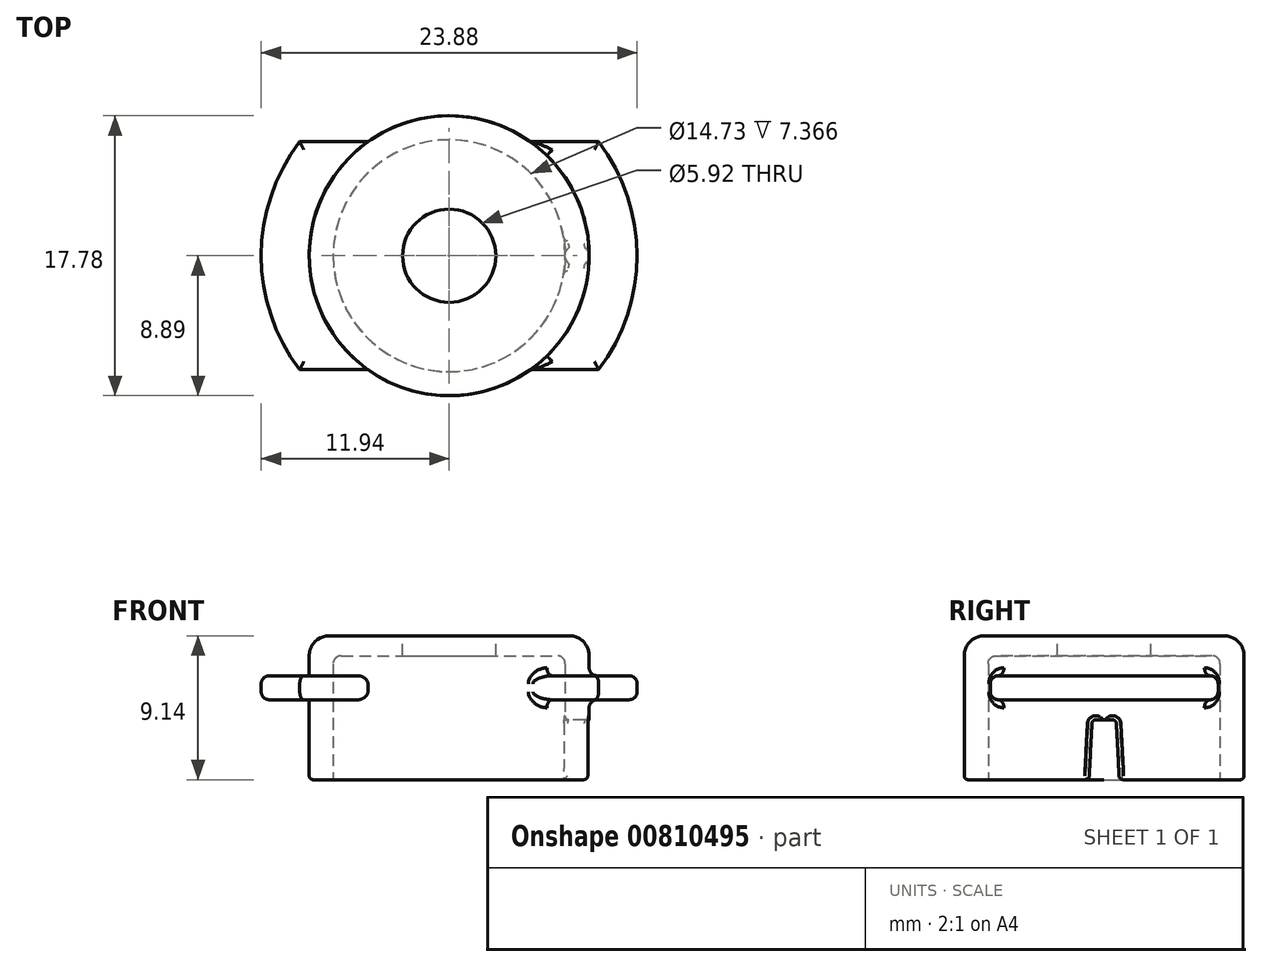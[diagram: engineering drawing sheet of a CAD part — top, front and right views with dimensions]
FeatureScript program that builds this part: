
annotation { "Feature Type Name" : "Feature", "Feature Type Description" : "" }
export const myFeature = defineFeature(function(context is Context, id is Id, definition is map)
    precondition{}
    {
        {
            var Q0;
            Q0=qCreatedBy(makeId("Top.planeOp"),FACE);
            var sketch = newSketch(context, id + "F0", { "sketchPlane" : qUnion([Q0])});
            skCircle(sketch, "E0", {"center": v(0, 0) * mm, "radius": 11.94 * mm});
            skSolve(sketch);
        }
        {
            var Q0;
            Q0=makeQuery(id+"F0.imprint","IMPRINT",FACE,{"disambiguationData":[TD([[makeQuery(id+"F0.imprint","IMPRINT",EDGE,{"derivedFrom":sQuery(id+"F0.wireOp",EDGE,"E0")}),1.0]])]});
            var sketch = newSketch(context, id + "F1", { "sketchPlane" : qUnion([Q0])});
            skLineSegment(sketch, "E1", {"start": v(9.5, 7.24) * mm, "end": v(-9.5, 7.24) * mm});
            skLineSegment(sketch, "E2", {"start": v(9.5, -7.24) * mm, "end": v(-9.5, -7.24) * mm});
            skLineSegment(sketch, "E3", {"start": v(-9.5, 7.24) * mm, "end": v(-9.5, -7.24) * mm, "construction": true});
            skLineSegment(sketch, "E4", {"start": v(9.5, 7.24) * mm, "end": v(9.5, -7.24) * mm, "construction": true});
            skSolve(sketch);
        }
        {
            var Q0;
            Q0=qSketchRegion(id+"F0",true);
            extrude(context, id + "F2", {"entities" : qUnion([Q0]), "depth" : 1.52 * mm, "offsetDistance" : 25.4 * mm});
        }
        {
            var Q0;
            {var subQ0=sQuery(id+"F1.wireOp",EDGE,"E1");Q0=makeQuery(id+"F1.imprint","IMPRINT",FACE,{"disambiguationData":[TD([[makeQuery(id+"F1.imprint","IMPRINT",EDGE,{"derivedFrom":subQ0}),-1.0]])]});}
            var Q1;
            {var subQ0=sQuery(id+"F1.wireOp",EDGE,"E2");Q1=makeQuery(id+"F1.imprint","IMPRINT",FACE,{"disambiguationData":[TD([[makeQuery(id+"F1.imprint","IMPRINT",EDGE,{"derivedFrom":subQ0}),1.0]])]});}
            extrude(context, id + "F3", {"entities" : qUnion([Q0, Q1]), "operationType" : NewBodyOperationType.REMOVE, "depth" : 2.54 * mm, "offsetDistance" : 25.4 * mm, "hasSecondDirection" : true, "secondDirectionOppositeDirection" : true, "secondDirectionDepth" : 25.4 * mm});
        }
        {
            var Q0;
            Q0=makeQuery(id+"F2.opExtrude","CAP_FACE",FACE,{"disambiguationData":[OSD([sQuery(id+"F0.wireOp",EDGE,"E0")])],"isStart":true});
            var sketch = newSketch(context, id + "F4", { "sketchPlane" : qUnion([Q0])});
            skCircle(sketch, "E5", {"center": v(0, 0) * mm, "radius": 8.9 * mm});
            skSolve(sketch);
        }
        {
            var Q0;
            Q0=qSketchRegion(id+"F4",true);
            extrude(context, id + "F5", {"entities" : qUnion([Q0]), "operationType" : NewBodyOperationType.ADD, "oppositeDirection" : true, "depth" : 1.52 * mm, "offsetDistance" : 25.4 * mm});
        }
        {
            var Q0;
            Q0=makeQuery(id+"F5.boolean.opBoolean","MERGE",FACE,{"derivedFrom":[makeQuery(id+"F2.opExtrude","CAP_FACE",FACE,{"disambiguationData":[OSD([sQuery(id+"F0.wireOp",EDGE,"E0")])],"isStart":true}),makeQuery(id+"F5.opExtrude","CAP_FACE",FACE,{"disambiguationData":[OSD([sQuery(id+"F4.wireOp",EDGE,"E5")])],"isStart":true})]});
            var sketch = newSketch(context, id + "F6", { "sketchPlane" : qUnion([Q0])});
            skCircle(sketch, "E6", {"center": v(0, 0) * mm, "radius": 8.9 * mm});
            skSolve(sketch);
        }
        {
            var Q0;
            Q0=qSketchRegion(id+"F6",true);
            extrude(context, id + "F7", {"entities" : qUnion([Q0]), "operationType" : NewBodyOperationType.ADD, "depth" : 5.08 * mm, "offsetDistance" : 25.4 * mm});
        }
        {
            var Q0;
            Q0=makeQuery(id+"F7.opExtrude","CAP_FACE",FACE,{"disambiguationData":[OSD([sQuery(id+"F6.wireOp",EDGE,"E6")])],"isStart":false});
            var sketch = newSketch(context, id + "F8", { "sketchPlane" : qUnion([Q0])});
            skCircle(sketch, "E7", {"center": v(0, 0) * mm, "radius": 7.37 * mm});
            skSolve(sketch);
        }
        {
            var Q0;
            Q0=qSketchRegion(id+"F8",true);
            extrude(context, id + "F9", {"entities" : qUnion([Q0]), "operationType" : NewBodyOperationType.REMOVE, "oppositeDirection" : true, "depth" : 5.08 * mm, "offsetDistance" : 25.4 * mm});
        }
        {
            var Q0;
            Q0=qCreatedBy(makeId("Front.planeOp"),FACE);
            var sketch = newSketch(context, id + "F10", { "sketchPlane" : qUnion([Q0])});
            skLineSegment(sketch, "E8", {"start": v(0, 0) * mm, "end": v(0, -7.62) * mm, "construction": true});
            skSolve(sketch);
        }
        {
            var Q0;
            Q0=makeQuery(id+"F9.boolean.opBoolean","COPY",FACE,{"derivedFrom":makeQuery(id+"F9.opExtrude","CAP_FACE",FACE,{"disambiguationData":[OSD([sQuery(id+"F8.wireOp",EDGE,"E7")])],"isStart":false})});
            var sketch = newSketch(context, id + "F11", { "sketchPlane" : qUnion([Q0])});
            skCircle(sketch, "E9", {"center": v(0, 0) * mm, "radius": 7.37 * mm});
            skSolve(sketch);
        }
        {
            var Q0;
            Q0=makeQuery(id+"F5.boolean.opBoolean","MERGE",FACE,{"derivedFrom":[makeQuery(id+"F2.opExtrude","CAP_FACE",FACE,{"disambiguationData":[OSD([sQuery(id+"F0.wireOp",EDGE,"E0")])],"isStart":false}),makeQuery(id+"F5.opExtrude","CAP_FACE",FACE,{"disambiguationData":[OSD([sQuery(id+"F4.wireOp",EDGE,"E5")])],"isStart":false})]});
            var sketch = newSketch(context, id + "F12", { "sketchPlane" : qUnion([Q0])});
            skCircle(sketch, "E10", {"center": v(0, 0) * mm, "radius": 8.9 * mm});
            skSolve(sketch);
        }
        {
            var Q0;
            Q0 = qSketchRegion(id + "F12", true);
            extrude(context, id + "F13", {"entities" : qUnion([Q0]), "operationType" : NewBodyOperationType.ADD, "depth" : 2.54 * mm, "offsetDistance" : 25.4 * mm});
        }
        {
            var Q0;
            Q0=makeQuery(id+"F13.opExtrude","CAP_FACE",FACE,{"disambiguationData":[OSD([sQuery(id+"F12.wireOp",EDGE,"E10")])],"isStart":false});
            var sketch = newSketch(context, id + "F14", { "sketchPlane" : qUnion([Q0])});
            skCircle(sketch, "E11", {"center": v(0, 0) * mm, "radius": 2.96 * mm});
            skSolve(sketch);
        }
        {
            var Q0;
            Q0 = qSketchRegion(id + "F14", true);
            extrude(context, id + "F15", {"entities" : qUnion([Q0]), "operationType" : NewBodyOperationType.REMOVE, "oppositeDirection" : true, "depth" : 25.4 * mm, "offsetDistance" : 25.4 * mm, "hasSecondDirection" : true, "secondDirectionOppositeDirection" : false, "secondDirectionDepth" : 25.4 * mm});
        }
        {
            var Q0;
            Q0=makeQuery(id+"F5.boolean.opBoolean","SPLIT",EDGE,{"disambiguationData":[OD(1.0)],"derivedFrom":makeQuery(id+"F3.boolean.opBoolean","INTERSECT",EDGE,{"derivedFrom":[makeQuery(id+"F2.opExtrude","CAP_FACE",FACE,{"disambiguationData":[OSD([sQuery(id+"F0.wireOp",EDGE,"E0")])],"isStart":false}),makeQuery(id+"F3.opExtrude","SWEPT_FACE",FACE,{"disambiguationData":[OSD([sQuery(id+"F1.wireOp",EDGE,"E2")])]})]})});
            var Q1;
            Q1=makeQuery(id+"F5.boolean.opBoolean","SPLIT",EDGE,{"disambiguationData":[OD(1.0)],"derivedFrom":makeQuery(id+"F3.boolean.opBoolean","INTERSECT",EDGE,{"derivedFrom":[makeQuery(id+"F2.opExtrude","CAP_FACE",FACE,{"disambiguationData":[OSD([sQuery(id+"F0.wireOp",EDGE,"E0")])],"isStart":true}),makeQuery(id+"F3.opExtrude","SWEPT_FACE",FACE,{"disambiguationData":[OSD([sQuery(id+"F1.wireOp",EDGE,"E2")])]})]})});
            var Q2;
            Q2=makeQuery(id+"F3.boolean.opBoolean","SPLIT",EDGE,{"disambiguationData":[OD(1.0)],"derivedFrom":makeQuery(id+"F2.opExtrude","CAP_EDGE",EDGE,{"disambiguationData":[OSD([sQuery(id+"F0.wireOp",EDGE,"E0")])],"isStart":true})});
            var Q3;
            Q3=makeQuery(id+"F3.boolean.opBoolean","SPLIT",EDGE,{"disambiguationData":[OD(1.0)],"derivedFrom":makeQuery(id+"F2.opExtrude","CAP_EDGE",EDGE,{"disambiguationData":[OSD([sQuery(id+"F0.wireOp",EDGE,"E0")])],"isStart":false})});
            var Q4;
            Q4=makeQuery(id+"F5.boolean.opBoolean","SPLIT",EDGE,{"disambiguationData":[OD(1.0)],"derivedFrom":makeQuery(id+"F3.boolean.opBoolean","INTERSECT",EDGE,{"derivedFrom":[makeQuery(id+"F2.opExtrude","CAP_FACE",FACE,{"disambiguationData":[OSD([sQuery(id+"F0.wireOp",EDGE,"E0")])],"isStart":true}),makeQuery(id+"F3.opExtrude","SWEPT_FACE",FACE,{"disambiguationData":[OSD([sQuery(id+"F1.wireOp",EDGE,"E1")])]})]})});
            var Q5;
            Q5=makeQuery(id+"F5.boolean.opBoolean","SPLIT",EDGE,{"disambiguationData":[OD(1.0)],"derivedFrom":makeQuery(id+"F3.boolean.opBoolean","INTERSECT",EDGE,{"derivedFrom":[makeQuery(id+"F2.opExtrude","CAP_FACE",FACE,{"disambiguationData":[OSD([sQuery(id+"F0.wireOp",EDGE,"E0")])],"isStart":false}),makeQuery(id+"F3.opExtrude","SWEPT_FACE",FACE,{"disambiguationData":[OSD([sQuery(id+"F1.wireOp",EDGE,"E1")])]})]})});
            var Q6;
            Q6=makeQuery(id+"F5.boolean.opBoolean","SPLIT",EDGE,{"disambiguationData":[OD(0.0)],"derivedFrom":makeQuery(id+"F3.boolean.opBoolean","INTERSECT",EDGE,{"derivedFrom":[makeQuery(id+"F2.opExtrude","CAP_FACE",FACE,{"disambiguationData":[OSD([sQuery(id+"F0.wireOp",EDGE,"E0")])],"isStart":true}),makeQuery(id+"F3.opExtrude","SWEPT_FACE",FACE,{"disambiguationData":[OSD([sQuery(id+"F1.wireOp",EDGE,"E2")])]})]})});
            var Q7;
            Q7=makeQuery(id+"F5.boolean.opBoolean","SPLIT",EDGE,{"disambiguationData":[OD(0.0)],"derivedFrom":makeQuery(id+"F3.boolean.opBoolean","INTERSECT",EDGE,{"derivedFrom":[makeQuery(id+"F2.opExtrude","CAP_FACE",FACE,{"disambiguationData":[OSD([sQuery(id+"F0.wireOp",EDGE,"E0")])],"isStart":false}),makeQuery(id+"F3.opExtrude","SWEPT_FACE",FACE,{"disambiguationData":[OSD([sQuery(id+"F1.wireOp",EDGE,"E2")])]})]})});
            var Q8;
            Q8=makeQuery(id+"F3.boolean.opBoolean","SPLIT",EDGE,{"disambiguationData":[OD(0.0)],"derivedFrom":makeQuery(id+"F2.opExtrude","CAP_EDGE",EDGE,{"disambiguationData":[OSD([sQuery(id+"F0.wireOp",EDGE,"E0")])],"isStart":true})});
            var Q9;
            Q9=makeQuery(id+"F3.boolean.opBoolean","SPLIT",EDGE,{"disambiguationData":[OD(0.0)],"derivedFrom":makeQuery(id+"F2.opExtrude","CAP_EDGE",EDGE,{"disambiguationData":[OSD([sQuery(id+"F0.wireOp",EDGE,"E0")])],"isStart":false})});
            var Q10;
            Q10=makeQuery(id+"F5.boolean.opBoolean","SPLIT",EDGE,{"disambiguationData":[OD(0.0)],"derivedFrom":makeQuery(id+"F3.boolean.opBoolean","INTERSECT",EDGE,{"derivedFrom":[makeQuery(id+"F2.opExtrude","CAP_FACE",FACE,{"disambiguationData":[OSD([sQuery(id+"F0.wireOp",EDGE,"E0")])],"isStart":false}),makeQuery(id+"F3.opExtrude","SWEPT_FACE",FACE,{"disambiguationData":[OSD([sQuery(id+"F1.wireOp",EDGE,"E1")])]})]})});
            var Q11;
            Q11=makeQuery(id+"F5.boolean.opBoolean","SPLIT",EDGE,{"disambiguationData":[OD(0.0)],"derivedFrom":makeQuery(id+"F3.boolean.opBoolean","INTERSECT",EDGE,{"derivedFrom":[makeQuery(id+"F2.opExtrude","CAP_FACE",FACE,{"disambiguationData":[OSD([sQuery(id+"F0.wireOp",EDGE,"E0")])],"isStart":true}),makeQuery(id+"F3.opExtrude","SWEPT_FACE",FACE,{"disambiguationData":[OSD([sQuery(id+"F1.wireOp",EDGE,"E1")])]})]})});
            fillet(context, id + "F16", {"entities" : qUnion([Q0, Q1, Q2, Q3, Q4, Q5, Q6, Q7, Q8, Q9, Q10, Q11]), "radius" : 0.5 * mm, "tangentPropagation" : true, "allowEdgeOverflow" : false});
        }
        {
            var Q0;
            Q0=makeQuery(id+"F13.opExtrude","CAP_EDGE",EDGE,{"disambiguationData":[OSD([sQuery(id+"F12.wireOp",EDGE,"E10")])],"isStart":false});
            fillet(context, id + "F17", {"entities" : qUnion([Q0]), "radius" : 1.27 * mm, "tangentPropagation" : true, "allowEdgeOverflow" : false});
        }
        {
            var Q0;
            Q0=makeQuery(id+"F11.imprint","IMPRINT",FACE,{"disambiguationData":[TD([[makeQuery(id+"F11.imprint","IMPRINT",EDGE,{"derivedFrom":sQuery(id+"F11.wireOp",EDGE,"E9")}),1.0]])]});
            var sketch = newSketch(context, id + "F18", { "sketchPlane" : qUnion([Q0])});
            skCircle(sketch, "E12", {"center": v(0, 0) * mm, "radius": 7.37 * mm});
            skSolve(sketch);
        }
        {
            var Q0;
            Q0 = qSketchRegion(id + "F18", true);
            extrude(context, id + "F19", {"entities" : qUnion([Q0]), "operationType" : NewBodyOperationType.REMOVE, "oppositeDirection" : true, "depth" : 2.8 * mm, "offsetDistance" : 25.4 * mm});
        }
        {
            var Q0;
            Q0=makeQuery(id+"F13.opExtrude","CAP_FACE",FACE,{"disambiguationData":[OSD([sQuery(id+"F12.wireOp",EDGE,"E10")])],"isStart":false});
            cPlane(context, id + "F20", {"entities" : qUnion([Q0]), "cplaneType" : CPlaneType.OFFSET, "offset" : 5.33 * mm, "oppositeDirection" : true, "width" : 152.4 * mm, "height" : 152.4 * mm});
        }
        {
            var Q0;
            Q0=qCreatedBy(id+"F20.planeOp",FACE);
            var sketch = newSketch(context, id + "F21", { "sketchPlane" : qUnion([Q0])});
            skLineSegment(sketch, "E13", {"start": v(8.86, 0.76) * mm, "end": v(7.33, 0.76) * mm});
            skLineSegment(sketch, "E14", {"start": v(8.86, -0.76) * mm, "end": v(7.33, -0.76) * mm});
            skLineSegment(sketch, "E15", {"start": v(0, 0) * mm, "end": v(8.9, 0) * mm, "construction": true});
            skArc(sketch, "E16", {"start": v(7.33, 0.76) * mm, "mid": v(7.37, 0) * mm, "end": v(7.33, -0.76) * mm});
            skArc(sketch, "E17", {"start": v(8.86, 0.76) * mm, "mid": v(8.9, 0) * mm, "end": v(8.86, -0.76) * mm});
            skSolve(sketch);
        }
        {
            var Q0;
            Q0 = qSketchRegion(id + "F21", true);
            extrude(context, id + "F22", {"entities" : qUnion([Q0]), "operationType" : NewBodyOperationType.REMOVE, "oppositeDirection" : true, "depth" : 25.4 * mm, "offsetDistance" : 25.4 * mm, "hasDraft" : true, "draftAngle" : 3 * degree});
        }
        {
            var Q0;
            Q0=makeQuery(id+"F22.boolean.opBoolean","COPY",EDGE,{"derivedFrom":makeQuery(id+"F22.opExtrude","CAP_EDGE",EDGE,{"disambiguationData":[OSD([sQuery(id+"F21.wireOp",EDGE,"E17")])],"isStart":true})});
            var Q1;
            {var subQ2=sQuery(id+"F4.wireOp",EDGE,"E5");var subQ6=makeQuery(id+"F5.opExtrude","SWEPT_FACE",FACE,{"disambiguationData":[OSD([subQ2])]});Q1=makeQuery(id+"F22.boolean.opBoolean","INTERSECT",EDGE,{"derivedFrom":[makeQuery(id+"F13.boolean.opBoolean","MERGE",FACE,{"derivedFrom":[makeQuery(id+"F7.boolean.opBoolean","MERGE",FACE,{"derivedFrom":[makeQuery(id+"F5.boolean.opBoolean","SPLIT",FACE,{"disambiguationData":[TD([makeQuery(id+"F3.boolean.opBoolean","COPY",FACE,{"derivedFrom":makeQuery(id+"F3.opExtrude","SWEPT_FACE",FACE,{"disambiguationData":[OSD([sQuery(id+"F1.wireOp",EDGE,"E1")])]})})])],"derivedFrom":subQ6}),makeQuery(id+"F5.boolean.opBoolean","SPLIT",FACE,{"disambiguationData":[TD([makeQuery(id+"F3.boolean.opBoolean","COPY",FACE,{"derivedFrom":makeQuery(id+"F3.opExtrude","SWEPT_FACE",FACE,{"disambiguationData":[OSD([sQuery(id+"F1.wireOp",EDGE,"E2")])]})})])],"derivedFrom":subQ6}),makeQuery(id+"F7.opExtrude","SWEPT_FACE",FACE,{"disambiguationData":[OSD([sQuery(id+"F6.wireOp",EDGE,"E6")])]})]}),makeQuery(id+"F13.opExtrude","SWEPT_FACE",FACE,{"disambiguationData":[OSD([sQuery(id+"F12.wireOp",EDGE,"E10")])]})]}),makeQuery(id+"F22.opExtrude","SWEPT_FACE",FACE,{"disambiguationData":[OSD([sQuery(id+"F21.wireOp",EDGE,"E14")])]})]});}
            var Q2;
            {var subQ2=sQuery(id+"F4.wireOp",EDGE,"E5");var subQ6=makeQuery(id+"F5.opExtrude","SWEPT_FACE",FACE,{"disambiguationData":[OSD([subQ2])]});Q2=makeQuery(id+"F22.boolean.opBoolean","INTERSECT",EDGE,{"derivedFrom":[makeQuery(id+"F13.boolean.opBoolean","MERGE",FACE,{"derivedFrom":[makeQuery(id+"F7.boolean.opBoolean","MERGE",FACE,{"derivedFrom":[makeQuery(id+"F5.boolean.opBoolean","SPLIT",FACE,{"disambiguationData":[TD([makeQuery(id+"F3.boolean.opBoolean","COPY",FACE,{"derivedFrom":makeQuery(id+"F3.opExtrude","SWEPT_FACE",FACE,{"disambiguationData":[OSD([sQuery(id+"F1.wireOp",EDGE,"E1")])]})})])],"derivedFrom":subQ6}),makeQuery(id+"F5.boolean.opBoolean","SPLIT",FACE,{"disambiguationData":[TD([makeQuery(id+"F3.boolean.opBoolean","COPY",FACE,{"derivedFrom":makeQuery(id+"F3.opExtrude","SWEPT_FACE",FACE,{"disambiguationData":[OSD([sQuery(id+"F1.wireOp",EDGE,"E2")])]})})])],"derivedFrom":subQ6}),makeQuery(id+"F7.opExtrude","SWEPT_FACE",FACE,{"disambiguationData":[OSD([sQuery(id+"F6.wireOp",EDGE,"E6")])]})]}),makeQuery(id+"F13.opExtrude","SWEPT_FACE",FACE,{"disambiguationData":[OSD([sQuery(id+"F12.wireOp",EDGE,"E10")])]})]}),makeQuery(id+"F22.opExtrude","SWEPT_FACE",FACE,{"disambiguationData":[OSD([sQuery(id+"F21.wireOp",EDGE,"E13")])]})]});}
            var Q3;
            Q3=makeQuery(id+"F22.boolean.opBoolean","INTERSECT",EDGE,{"derivedFrom":[makeQuery(id+"F19.boolean.opBoolean","MERGE",FACE,{"derivedFrom":[makeQuery(id+"F9.boolean.opBoolean","COPY",FACE,{"derivedFrom":makeQuery(id+"F9.opExtrude","SWEPT_FACE",FACE,{"disambiguationData":[OSD([sQuery(id+"F8.wireOp",EDGE,"E7")])]})}),makeQuery(id+"F19.opExtrude","SWEPT_FACE",FACE,{"disambiguationData":[OSD([sQuery(id+"F18.wireOp",EDGE,"E12")])]})]}),makeQuery(id+"F22.opExtrude","SWEPT_FACE",FACE,{"disambiguationData":[OSD([sQuery(id+"F21.wireOp",EDGE,"E14")])]})]});
            var Q4;
            Q4=makeQuery(id+"F22.boolean.opBoolean","INTERSECT",EDGE,{"derivedFrom":[makeQuery(id+"F19.boolean.opBoolean","MERGE",FACE,{"derivedFrom":[makeQuery(id+"F9.boolean.opBoolean","COPY",FACE,{"derivedFrom":makeQuery(id+"F9.opExtrude","SWEPT_FACE",FACE,{"disambiguationData":[OSD([sQuery(id+"F8.wireOp",EDGE,"E7")])]})}),makeQuery(id+"F19.opExtrude","SWEPT_FACE",FACE,{"disambiguationData":[OSD([sQuery(id+"F18.wireOp",EDGE,"E12")])]})]}),makeQuery(id+"F22.opExtrude","SWEPT_FACE",FACE,{"disambiguationData":[OSD([sQuery(id+"F21.wireOp",EDGE,"E13")])]})]});
            var Q5;
            Q5=makeQuery(id+"F22.boolean.opBoolean","COPY",EDGE,{"derivedFrom":makeQuery(id+"F22.opExtrude","CAP_EDGE",EDGE,{"disambiguationData":[OSD([sQuery(id+"F21.wireOp",EDGE,"E16")])],"isStart":true})});
            var Q6;
            Q6=makeQuery(id+"F22.boolean.opBoolean","COPY",EDGE,{"derivedFrom":makeQuery(id+"F22.opExtrude","CAP_EDGE",EDGE,{"disambiguationData":[OSD([sQuery(id+"F21.wireOp",EDGE,"E14")])],"isStart":true})});
            var Q7;
            Q7=makeQuery(id+"F22.boolean.opBoolean","COPY",EDGE,{"derivedFrom":makeQuery(id+"F22.opExtrude","CAP_EDGE",EDGE,{"disambiguationData":[OSD([sQuery(id+"F21.wireOp",EDGE,"E13")])],"isStart":true})});
            var Q8;
            Q8=makeQuery(id+"F22.boolean.opBoolean","INTERSECT",EDGE,{"derivedFrom":[makeQuery(id+"F7.opExtrude","CAP_FACE",FACE,{"disambiguationData":[OSD([sQuery(id+"F6.wireOp",EDGE,"E6")])],"isStart":false}),makeQuery(id+"F22.opExtrude","SWEPT_FACE",FACE,{"disambiguationData":[OSD([sQuery(id+"F21.wireOp",EDGE,"E14")])]})]});
            var Q9;
            Q9=makeQuery(id+"F22.boolean.opBoolean","INTERSECT",EDGE,{"derivedFrom":[makeQuery(id+"F7.opExtrude","CAP_FACE",FACE,{"disambiguationData":[OSD([sQuery(id+"F6.wireOp",EDGE,"E6")])],"isStart":false}),makeQuery(id+"F22.opExtrude","SWEPT_FACE",FACE,{"disambiguationData":[OSD([sQuery(id+"F21.wireOp",EDGE,"E13")])]})]});
            fillet(context, id + "F23", {"entities" : qUnion([Q0, Q1, Q2, Q3, Q4, Q5, Q6, Q7, Q8, Q9]), "radius" : 0.25 * mm, "tangentPropagation" : true, "allowEdgeOverflow" : false});
        }
        {
            var Q0;
            {var subQ1=sQuery(id+"F8.wireOp",EDGE,"E7");Q0=makeQuery(id+"FQYb2V3vegdUbzZ_1.1.F22.boolean.opBoolean","SPLIT",EDGE,{"disambiguationData":[TD([makeQuery(id+"FQYb2V3vegdUbzZ_1.1.F22.opExtrude","SWEPT_FACE",FACE,{"disambiguationData":[OSD([sQuery(id+"F21.wireOp",EDGE,"E13")])]})])],"derivedFrom":makeQuery(id+"F9.boolean.opBoolean","COPY",EDGE,{"derivedFrom":makeQuery(id+"F9.opExtrude","CAP_EDGE",EDGE,{"disambiguationData":[OSD([subQ1])],"isStart":true})})});}
            var Q1;
            {var subQ1=sQuery(id+"F6.wireOp",EDGE,"E6");Q1=makeQuery(id+"FQYb2V3vegdUbzZ_1.1.F22.boolean.opBoolean","SPLIT",EDGE,{"disambiguationData":[TD([makeQuery(id+"FQYb2V3vegdUbzZ_1.1.F22.opExtrude","SWEPT_FACE",FACE,{"disambiguationData":[OSD([sQuery(id+"F21.wireOp",EDGE,"E13")])]})])],"derivedFrom":makeQuery(id+"F7.opExtrude","CAP_EDGE",EDGE,{"disambiguationData":[OSD([subQ1])],"isStart":false})});}
            var Q2;
            {var subQ1=sQuery(id+"F21.wireOp",EDGE,"E14");var subQ3=sQuery(id+"F8.wireOp",EDGE,"E7");var subQ5=sQuery(id+"F21.wireOp",EDGE,"E13");Q2=makeQuery(id+"FQYb2V3vegdUbzZ_1.2.F22.boolean.opBoolean","SPLIT",EDGE,{"disambiguationData":[TD([makeQuery(id+"FQYb2V3vegdUbzZ_1.2.F22.opExtrude","SWEPT_FACE",FACE,{"disambiguationData":[OSD([subQ5])]})])],"derivedFrom":makeQuery(id+"FQYb2V3vegdUbzZ_1.1.F22.boolean.opBoolean","SPLIT",EDGE,{"disambiguationData":[TD([makeQuery(id+"FQYb2V3vegdUbzZ_1.1.F22.opExtrude","SWEPT_FACE",FACE,{"disambiguationData":[OSD([subQ1])]})])],"derivedFrom":makeQuery(id+"F9.boolean.opBoolean","COPY",EDGE,{"derivedFrom":makeQuery(id+"F9.opExtrude","CAP_EDGE",EDGE,{"disambiguationData":[OSD([subQ3])],"isStart":true})})})});}
            var Q3;
            {var subQ2=sQuery(id+"F6.wireOp",EDGE,"E6");var subQ7=sQuery(id+"F21.wireOp",EDGE,"E13");var subQ8=sQuery(id+"F21.wireOp",EDGE,"E14");Q3=makeQuery(id+"FQYb2V3vegdUbzZ_1.2.F22.boolean.opBoolean","SPLIT",EDGE,{"disambiguationData":[TD([makeQuery(id+"FQYb2V3vegdUbzZ_1.2.F22.opExtrude","SWEPT_FACE",FACE,{"disambiguationData":[OSD([subQ7])]})])],"derivedFrom":makeQuery(id+"FQYb2V3vegdUbzZ_1.1.F22.boolean.opBoolean","SPLIT",EDGE,{"disambiguationData":[TD([makeQuery(id+"FQYb2V3vegdUbzZ_1.1.F22.opExtrude","SWEPT_FACE",FACE,{"disambiguationData":[OSD([subQ8])]})])],"derivedFrom":makeQuery(id+"F7.opExtrude","CAP_EDGE",EDGE,{"disambiguationData":[OSD([subQ2])],"isStart":false})})});}
            var Q4;
            {var subQ2=sQuery(id+"F6.wireOp",EDGE,"E6");var subQ4=sQuery(id+"F21.wireOp",EDGE,"E13");var subQ8=sQuery(id+"F21.wireOp",EDGE,"E14");Q4=makeQuery(id+"FQYb2V3vegdUbzZ_1.3.F22.boolean.opBoolean","SPLIT",EDGE,{"disambiguationData":[TD([makeQuery(id+"FQYb2V3vegdUbzZ_1.3.F22.opExtrude","SWEPT_FACE",FACE,{"disambiguationData":[OSD([subQ4])]})])],"derivedFrom":makeQuery(id+"FQYb2V3vegdUbzZ_1.2.F22.boolean.opBoolean","SPLIT",EDGE,{"disambiguationData":[TD([makeQuery(id+"FQYb2V3vegdUbzZ_1.2.F22.opExtrude","SWEPT_FACE",FACE,{"disambiguationData":[OSD([subQ8])]})])],"derivedFrom":makeQuery(id+"FQYb2V3vegdUbzZ_1.1.F22.boolean.opBoolean","SPLIT",EDGE,{"disambiguationData":[TD([makeQuery(id+"FQYb2V3vegdUbzZ_1.1.F22.opExtrude","SWEPT_FACE",FACE,{"disambiguationData":[OSD([subQ8])]})])],"derivedFrom":makeQuery(id+"F7.opExtrude","CAP_EDGE",EDGE,{"disambiguationData":[OSD([subQ2])],"isStart":false})})})});}
            var Q5;
            {var subQ0=sQuery(id+"F21.wireOp",EDGE,"E14");var subQ2=sQuery(id+"F8.wireOp",EDGE,"E7");var subQ6=sQuery(id+"F21.wireOp",EDGE,"E13");Q5=makeQuery(id+"FQYb2V3vegdUbzZ_1.3.F22.boolean.opBoolean","SPLIT",EDGE,{"disambiguationData":[TD([makeQuery(id+"FQYb2V3vegdUbzZ_1.3.F22.opExtrude","SWEPT_FACE",FACE,{"disambiguationData":[OSD([subQ6])]})])],"derivedFrom":makeQuery(id+"FQYb2V3vegdUbzZ_1.2.F22.boolean.opBoolean","SPLIT",EDGE,{"disambiguationData":[TD([makeQuery(id+"FQYb2V3vegdUbzZ_1.2.F22.opExtrude","SWEPT_FACE",FACE,{"disambiguationData":[OSD([subQ0])]})])],"derivedFrom":makeQuery(id+"FQYb2V3vegdUbzZ_1.1.F22.boolean.opBoolean","SPLIT",EDGE,{"disambiguationData":[TD([makeQuery(id+"FQYb2V3vegdUbzZ_1.1.F22.opExtrude","SWEPT_FACE",FACE,{"disambiguationData":[OSD([subQ0])]})])],"derivedFrom":makeQuery(id+"F9.boolean.opBoolean","COPY",EDGE,{"derivedFrom":makeQuery(id+"F9.opExtrude","CAP_EDGE",EDGE,{"disambiguationData":[OSD([subQ2])],"isStart":true})})})})});}
            var Q6;
            {var subQ3=sQuery(id+"F8.wireOp",EDGE,"E7");var subQ6=sQuery(id+"F21.wireOp",EDGE,"E14");Q6=makeQuery(id+"FQYb2V3vegdUbzZ_1.3.F22.boolean.opBoolean","SPLIT",EDGE,{"disambiguationData":[TD([makeQuery(id+"FQYb2V3vegdUbzZ_1.3.F22.opExtrude","SWEPT_FACE",FACE,{"disambiguationData":[OSD([subQ6])]})])],"derivedFrom":makeQuery(id+"FQYb2V3vegdUbzZ_1.2.F22.boolean.opBoolean","SPLIT",EDGE,{"disambiguationData":[TD([makeQuery(id+"FQYb2V3vegdUbzZ_1.2.F22.opExtrude","SWEPT_FACE",FACE,{"disambiguationData":[OSD([subQ6])]})])],"derivedFrom":makeQuery(id+"FQYb2V3vegdUbzZ_1.1.F22.boolean.opBoolean","SPLIT",EDGE,{"disambiguationData":[TD([makeQuery(id+"FQYb2V3vegdUbzZ_1.1.F22.opExtrude","SWEPT_FACE",FACE,{"disambiguationData":[OSD([subQ6])]})])],"derivedFrom":makeQuery(id+"F9.boolean.opBoolean","COPY",EDGE,{"derivedFrom":makeQuery(id+"F9.opExtrude","CAP_EDGE",EDGE,{"disambiguationData":[OSD([subQ3])],"isStart":true})})})})});}
            var Q7;
            {var subQ2=sQuery(id+"F6.wireOp",EDGE,"E6");var subQ8=sQuery(id+"F21.wireOp",EDGE,"E14");Q7=makeQuery(id+"FQYb2V3vegdUbzZ_1.3.F22.boolean.opBoolean","SPLIT",EDGE,{"disambiguationData":[TD([makeQuery(id+"FQYb2V3vegdUbzZ_1.3.F22.opExtrude","SWEPT_FACE",FACE,{"disambiguationData":[OSD([subQ8])]})])],"derivedFrom":makeQuery(id+"FQYb2V3vegdUbzZ_1.2.F22.boolean.opBoolean","SPLIT",EDGE,{"disambiguationData":[TD([makeQuery(id+"FQYb2V3vegdUbzZ_1.2.F22.opExtrude","SWEPT_FACE",FACE,{"disambiguationData":[OSD([subQ8])]})])],"derivedFrom":makeQuery(id+"FQYb2V3vegdUbzZ_1.1.F22.boolean.opBoolean","SPLIT",EDGE,{"disambiguationData":[TD([makeQuery(id+"FQYb2V3vegdUbzZ_1.1.F22.opExtrude","SWEPT_FACE",FACE,{"disambiguationData":[OSD([subQ8])]})])],"derivedFrom":makeQuery(id+"F7.opExtrude","CAP_EDGE",EDGE,{"disambiguationData":[OSD([subQ2])],"isStart":false})})})});}
            fillet(context, id + "F24", {"entities" : qUnion([Q0, Q1, Q2, Q3, Q4, Q5, Q6, Q7]), "radius" : 0.25 * mm, "tangentPropagation" : true, "allowEdgeOverflow" : false});
        }
        {
            var Q0;
            Q0=makeQuery(id+"F19.boolean.opBoolean","COPY",EDGE,{"derivedFrom":makeQuery(id+"F19.opExtrude","CAP_EDGE",EDGE,{"disambiguationData":[OSD([sQuery(id+"F18.wireOp",EDGE,"E12")])],"isStart":false})});
            var Q1;
            Q1=makeQuery(id+"F7.boolean.opBoolean","SPLIT",EDGE,{"disambiguationData":[OD(0.0)],"derivedFrom":makeQuery(id+"F7.opExtrude","CAP_EDGE",EDGE,{"disambiguationData":[OSD([sQuery(id+"F6.wireOp",EDGE,"E6")])],"isStart":true})});
            var Q2;
            Q2=makeQuery(id+"F7.boolean.opBoolean","SPLIT",EDGE,{"disambiguationData":[OD(1.0)],"derivedFrom":makeQuery(id+"F7.opExtrude","CAP_EDGE",EDGE,{"disambiguationData":[OSD([sQuery(id+"F6.wireOp",EDGE,"E6")])],"isStart":true})});
            fillet(context, id + "F25", {"entities" : qUnion([Q0, Q1, Q2]), "radius" : 0.5 * mm, "tangentPropagation" : true, "allowEdgeOverflow" : false});
        }
    });
